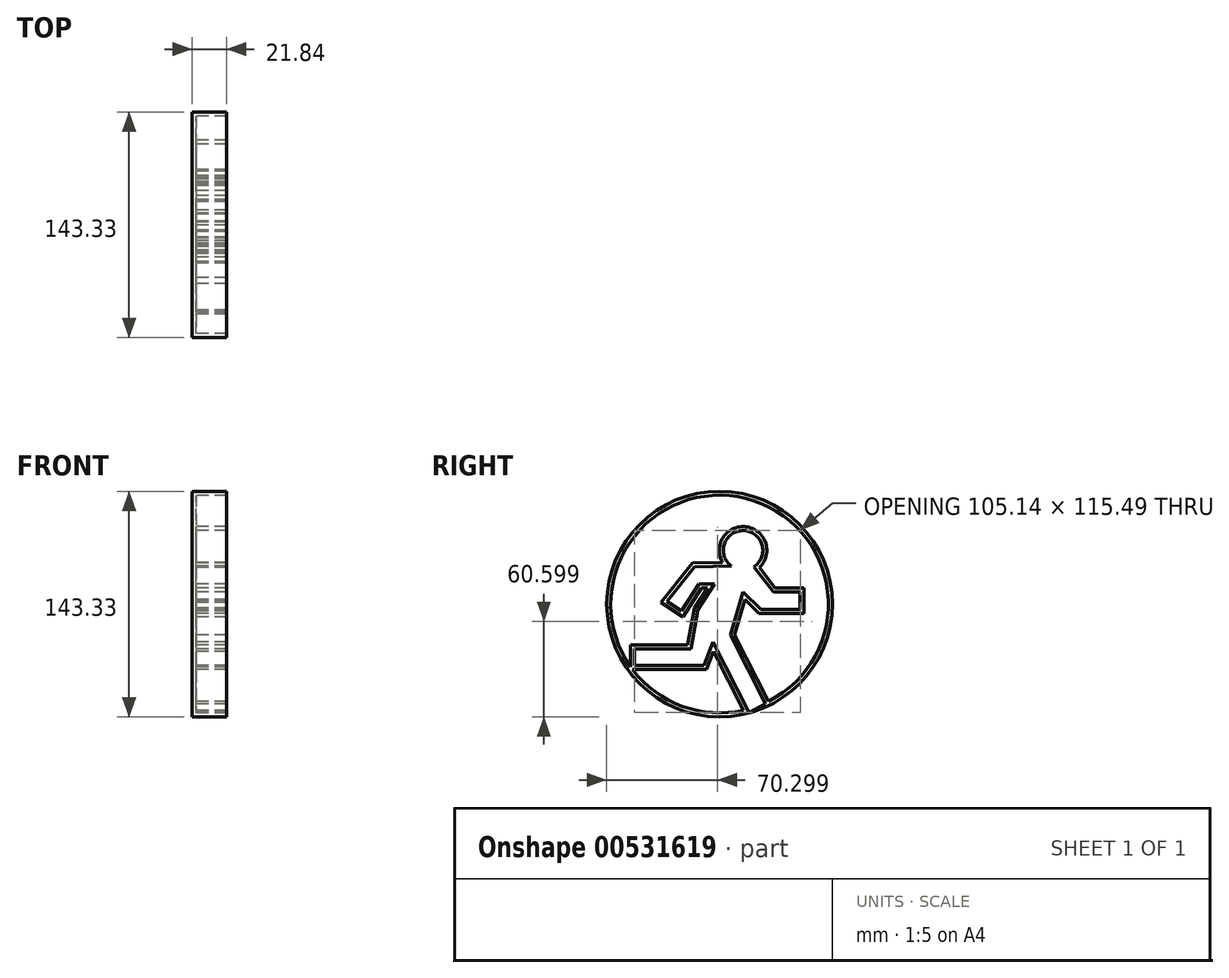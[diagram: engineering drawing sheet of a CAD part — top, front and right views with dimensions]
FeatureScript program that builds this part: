
annotation { "Feature Type Name" : "Feature", "Feature Type Description" : "" }
export const myFeature = defineFeature(function(context is Context, id is Id, definition is map)
    precondition{}
    {
        {
            var Q0;
            Q0=qCreatedBy(makeId("Right.planeOp"),FACE);
            var sketch = newSketch(context, id + "F0", { "sketchPlane" : qUnion([Q0])});
            skLineSegment(sketch, "E0", {"start": v(-94.12, 15.82) * mm, "end": v(-81.73, 0) * mm});
            skLineSegment(sketch, "E1", {"start": v(-81.73, 0) * mm, "end": v(-64.6, 0) * mm});
            skLineSegment(sketch, "E2", {"start": v(-64.6, 0) * mm, "end": v(-64.6, -11.28) * mm});
            skLineSegment(sketch, "E3", {"start": v(-64.6, -11.28) * mm, "end": v(-89.62, -11.28) * mm});
            skLineSegment(sketch, "E4", {"start": v(-89.62, -11.28) * mm, "end": v(-101.09, 0) * mm});
            skLineSegment(sketch, "E5", {"start": v(-101.09, 0) * mm, "end": v(-108.97, -27.5) * mm});
            skLineSegment(sketch, "E6", {"start": v(-108.97, -27.5) * mm, "end": v(-86.56, -71.23) * mm});
            skLineSegment(sketch, "E7", {"start": v(-86.56, -71.23) * mm, "end": v(-97.01, -76.59) * mm});
            skLineSegment(sketch, "E8", {"start": v(-97.01, -76.59) * mm, "end": v(-119.98, -31.76) * mm});
            skLineSegment(sketch, "E9", {"start": v(-119.98, -31.76) * mm, "end": v(-125.75, -46.85) * mm});
            skLineSegment(sketch, "E10", {"start": v(-125.75, -46.85) * mm, "end": v(-156.15, -46.85) * mm});
            skLineSegment(sketch, "E11", {"start": v(-156.15, -46.85) * mm, "end": v(-156.15, -36.3) * mm});
            skLineSegment(sketch, "E12", {"start": v(-156.15, -36.3) * mm, "end": v(-134.11, -36.3) * mm});
            skLineSegment(sketch, "E13", {"start": v(-134.11, -36.3) * mm, "end": v(-129.44, -11.28) * mm});
            skLineSegment(sketch, "E14", {"start": v(-129.44, -11.28) * mm, "end": v(-118.93, 4.85) * mm});
            skLineSegment(sketch, "E15", {"start": v(-118.93, 4.85) * mm, "end": v(-128.74, 4.85) * mm});
            skLineSegment(sketch, "E16", {"start": v(-128.74, 4.85) * mm, "end": v(-139.9, -12.3) * mm});
            skLineSegment(sketch, "E17", {"start": v(-139.9, -12.3) * mm, "end": v(-149.2, -6.24) * mm});
            skLineSegment(sketch, "E18", {"start": v(-149.2, -6.24) * mm, "end": v(-131.88, 15.82) * mm});
            skCircle(sketch, "E19", {"center": v(-115.8, -7.77) * mm, "radius": 71.67 * mm});
            skLineSegment(sketch, "E20", {"start": v(-156.15, -36.3) * mm, "end": v(-169.74, -36.3) * mm});
            skLineSegment(sketch, "E21", {"start": v(-169.74, -36.3) * mm, "end": v(-169.74, -46.85) * mm});
            skLineSegment(sketch, "E22", {"start": v(-169.74, -46.85) * mm, "end": v(-152.91, -46.85) * mm});
            skLineSegment(sketch, "E23", {"start": v(-131.88, 15.82) * mm, "end": v(-108.38, 16.31) * mm});
            skArc(sketch, "E24", {"start": v(-94.12, 15.82) * mm, "mid": v(-100.47, 38.9) * mm, "end": v(-108.38, 16.31) * mm});
            skSolve(sketch);
        }
        {
            var Q0;
            Q0=makeQuery(id+"F0.imprint","IMPRINT",FACE,{"disambiguationData":[TD([[makeQuery(id+"F0.imprint","IMPRINT",EDGE,{"derivedFrom":sQuery(id+"F0.wireOp",EDGE,"DbGwB71p-QBrX-K1cK-oAtP-Z7QaqoDUz7hQ")}),1.0]])]});
            var Q1;
            Q1=makeQuery(id+"F0.imprint","IMPRINT",FACE,{"disambiguationData":[TD([[makeQuery(id+"F0.imprint","IMPRINT",EDGE,{"derivedFrom":sQuery(id+"F0.wireOp",EDGE,"E0")}),1.0]])]});
            extrude(context, id + "F1", {"entities" : qUnion([Q0, Q1]), "depth" : 21.84 * mm, "offsetDistance" : 25.4 * mm});
        }
        {
            var Q0;
            Q0=makeQuery(id+"F1.opExtrude","CAP_FACE",FACE,{"disambiguationData":[OSD([sQuery(id+"F0.wireOp",EDGE,"DbGwB71p-QBrX-K1cK-oAtP-Z7QaqoDUz7hQ"),sQuery(id+"F0.wireOp",EDGE,"E0"),sQuery(id+"F0.wireOp",EDGE,"E1"),sQuery(id+"F0.wireOp",EDGE,"E2"),sQuery(id+"F0.wireOp",EDGE,"E3"),sQuery(id+"F0.wireOp",EDGE,"E4"),sQuery(id+"F0.wireOp",EDGE,"E5"),sQuery(id+"F0.wireOp",EDGE,"E6"),sQuery(id+"F0.wireOp",EDGE,"E7"),sQuery(id+"F0.wireOp",EDGE,"E8"),sQuery(id+"F0.wireOp",EDGE,"E9"),sQuery(id+"F0.wireOp",EDGE,"E10"),sQuery(id+"F0.wireOp",EDGE,"E12"),sQuery(id+"F0.wireOp",EDGE,"E13"),sQuery(id+"F0.wireOp",EDGE,"E14"),sQuery(id+"F0.wireOp",EDGE,"E15"),sQuery(id+"F0.wireOp",EDGE,"E16"),sQuery(id+"F0.wireOp",EDGE,"E17"),sQuery(id+"F0.wireOp",EDGE,"E18"),sQuery(id+"F0.wireOp",EDGE,"5dJhIVeO-OWxG-95OH-22Nz-T5d2C1ympByq"),sQuery(id+"F0.wireOp",EDGE,"E19"),sQuery(id+"F0.wireOp",EDGE,"E20"),sQuery(id+"F0.wireOp",EDGE,"E21"),sQuery(id+"F0.wireOp",EDGE,"E22")])],"isStart":false});
            shell(context, id + "F2", {"entities" : qUnion([Q0]), "thickness" : 2.54 * mm});
        }
    });
